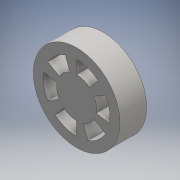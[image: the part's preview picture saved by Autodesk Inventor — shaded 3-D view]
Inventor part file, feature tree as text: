
AUTODESK INVENTOR PART (.ipt)
format: ipt  version: 2016 (Build 200138000, 138)  size: 132,608 bytes
history: native  units: mm
features: extrude x2, sketch x2, pattern_circular x1
ambient origin geometry x8: Origin, YZ Plane, XZ Plane, XY Plane, X Axis, Y Axis, Z Axis, Center Point
bodies: Solid1 (feature_tree)
feature tree (5):
  extrude  "Extrusion1"  Depth=40.0mm TaperAngle=0.0deg
  extrude  "Extrusion2"  Depth=30.0mm
  pattern_circular  "Circular Pattern1"  Count=5  [1 undecoded]
  sketch  "Sketch1"  dims[d0=130.0mm d1=40.0mm d2=0.0mm]
  sketch  "Sketch2"  dims[d4=6.981317mm d5=30.0mm d6=50.0mm d7=10.0mm d8=0.0mm d9=60.0mm d10=360.0deg]
note: 1 required parameter value undecoded (feature->parameter linkage not recoverable at this tier; creation-order binding heuristic only, values carry confidence <= 0.55)
